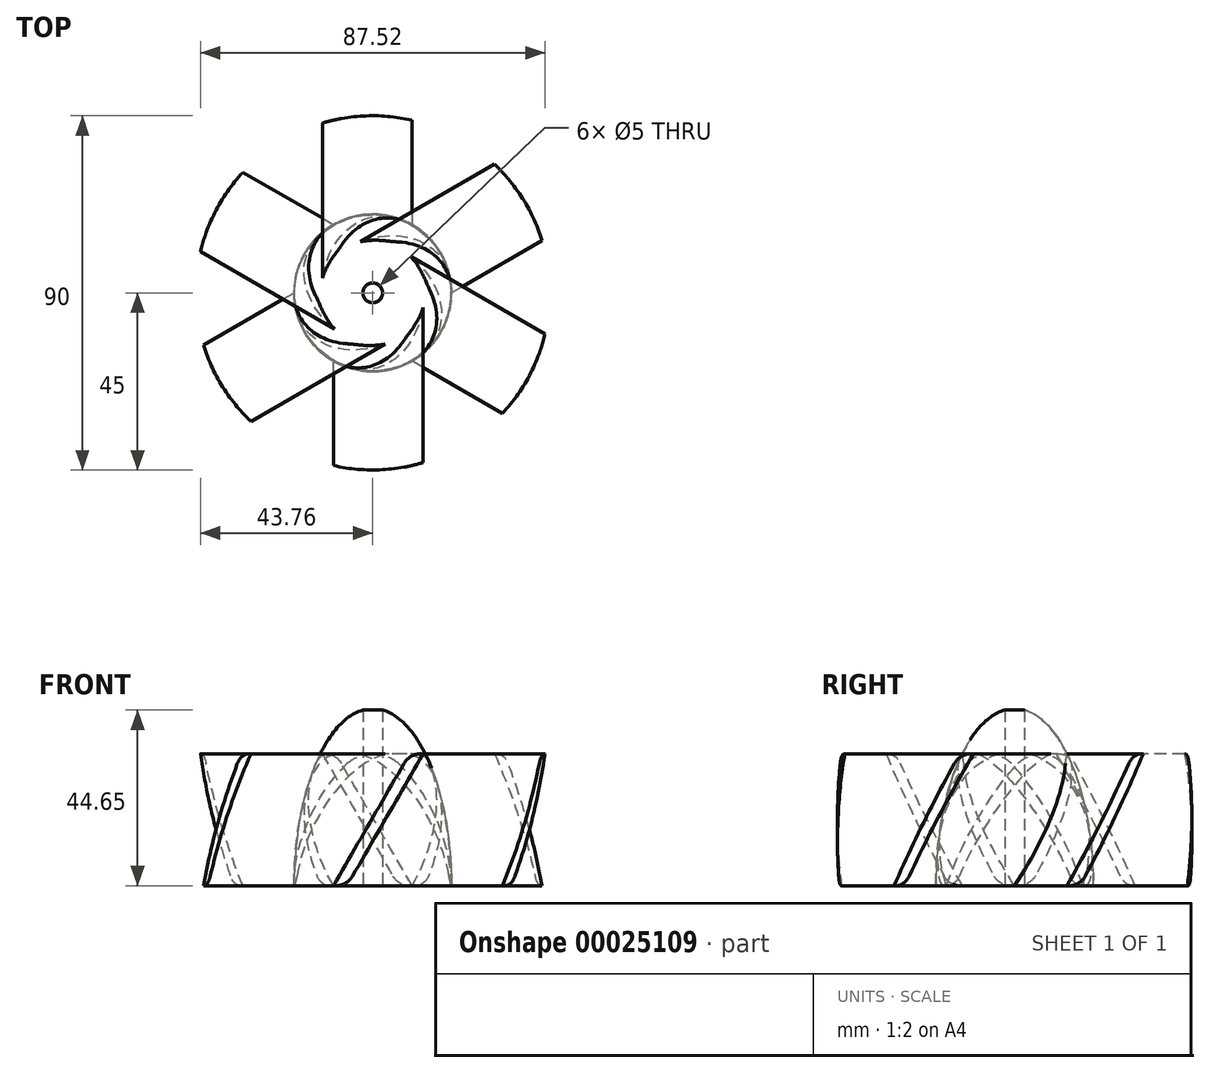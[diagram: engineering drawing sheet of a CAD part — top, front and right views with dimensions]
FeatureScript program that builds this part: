
annotation { "Feature Type Name" : "Feature", "Feature Type Description" : "" }
export const myFeature = defineFeature(function(context is Context, id is Id, definition is map)
    precondition{}
    {
        {
            var Q0;
            Q0=qCreatedBy(makeId("Front.planeOp"),FACE);
            var sketch = newSketch(context, id + "F0", { "sketchPlane" : qUnion([Q0])});
            skEllipticalArc(sketch, "E0", {});
            skLineSegment(sketch, "E1", {"start": v(-20, 0) * mm, "end": v(20, 0) * mm});
            skLineSegment(sketch, "E2", {"start": v(0, 0) * mm, "end": v(0, 45) * mm});
            const initialGuessF0  = {"E0": [0, 0, 0, 1, 0.045, 0.02, 4.71238898038469, 1.5707963267948966]};
            skSetInitialGuess(sketch, initialGuessF0);
            skSolve(sketch);
        }
        {
            var Q0;
            {var subQ0=sQuery(id+"F0.wireOp",EDGE,"E2");Q0=makeQuery(id+"F0.imprint","IMPRINT",FACE,{"disambiguationData":[TD([[makeQuery(id+"F0.imprint","IMPRINT",EDGE,{"derivedFrom":subQ0}),1.0]])]});}
            var Q1;
            Q1=sQuery(id+"F0.wireOp",EDGE,"E2");
            revolve(context, id + "F1", {"entities" : qUnion([Q0]), "axis" : qUnion([Q1]), "revolveType" : RevolveType.FULL});
        }
        {
            var Q0;
            Q0=qCreatedBy(makeId("Front.planeOp"),FACE);
            var sketch = newSketch(context, id + "F2", { "sketchPlane" : qUnion([Q0])});
            skLineSegment(sketch, "E3", {"start": v(-10, 0) * mm, "end": v(10.2, 35) * mm});
            skLineSegment(sketch, "E4", {"start": v(10.2, 35) * mm, "end": v(12.8, 33.5) * mm});
            skLineSegment(sketch, "E5", {"start": v(12.8, 33.5) * mm, "end": v(-6.54, 0) * mm});
            skLineSegment(sketch, "E6", {"start": v(-6.54, 0) * mm, "end": v(-10, 0) * mm});
            skSolve(sketch);
        }
        {
            var Q0;
            Q0 = qSketchRegion(id + "F2", true);
            extrude(context, id + "F3", {"entities" : qUnion([Q0]), "operationType" : NewBodyOperationType.ADD, "depth" : 50 * mm});
        }
        {
            var Q0;
            Q0=makeQuery(id+"F3.boolean.opBoolean","MERGE",FACE,{"derivedFrom":[makeQuery(id+"F1.opRevolve","SWEPT_FACE",FACE,{"disambiguationData":[OSD([sQuery(id+"F0.wireOp",EDGE,"E1")])]}),makeQuery(id+"F3.opExtrude","SWEPT_FACE",FACE,{"disambiguationData":[OSD([sQuery(id+"F2.wireOp",EDGE,"E6")])]})]});
            var sketch = newSketch(context, id + "F4", { "sketchPlane" : qUnion([Q0])});
            skCircle(sketch, "E7", {"center": v(0, 0) * mm, "radius": 55 * mm});
            skCircle(sketch, "E8", {"center": v(0, 0) * mm, "radius": 45 * mm});
            skSolve(sketch);
        }
        {
            var Q0;
            {var subQ0=sQuery(id+"F2.wireOp",EDGE,"E6");var subQ4=makeQuery(id+"F3.opExtrude","CAP_EDGE",EDGE,{"disambiguationData":[OSD([subQ0])],"isStart":false});Q0=makeQuery(id+"F4.imprint","IMPRINT",FACE,{"disambiguationData":[TD([[makeQuery(id+"F4.imprint","IMPRINT",EDGE,{"derivedFrom":subQ4}),1.0]])]});}
            var Q1;
            Q1=makeQuery(id+"F4.imprint","IMPRINT",FACE,{"disambiguationData":[TD([[makeQuery(id+"F4.imprint","IMPRINT",EDGE,{"derivedFrom":sQuery(id+"F4.wireOp",EDGE,"E7")}),1.0]])]});
            extrude(context, id + "F5", {"entities" : qUnion([Q0, Q1]), "operationType" : NewBodyOperationType.REMOVE, "oppositeDirection" : true, "depth" : 50 * mm});
        }
        {
            var Q0;
            Q0=makeQuery(id+"F3.opExtrude","SWEPT_EDGE",EDGE,{"disambiguationData":[OSD([sQuery(id+"F2.wireOp",EDGE,"E3"),sQuery(id+"F2.wireOp",EDGE,"E4")])]});
            var Q1;
            Q1=makeQuery(id+"F3.opExtrude","SWEPT_EDGE",EDGE,{"disambiguationData":[OSD([sQuery(id+"F2.wireOp",EDGE,"E5"),sQuery(id+"F2.wireOp",EDGE,"E6")])]});
            fillet(context, id + "F6", {"entities" : qUnion([Q0, Q1]), "radius" : 5 * mm, "tangentPropagation" : true, "allowEdgeOverflow" : false});
        }
        {
            var Q0;
            Q0=makeQuery(id+"F1.opRevolve","SWEPT_BODY",BODY,{"disambiguationData":[OSD([sQuery(id+"F0.wireOp",EDGE,"E0"),sQuery(id+"F0.wireOp",EDGE,"E1"),sQuery(id+"F0.wireOp",EDGE,"E2")])]});
            var Q1;
            Q1=makeQuery(id+"F1.opRevolve","SWEPT_EDGE",EDGE,{"disambiguationData":[OSD([sQuery(id+"F0.wireOp",EDGE,"E0"),sQuery(id+"F0.wireOp",EDGE,"E1")])]});
            circularPattern(context, id + "F7", {"entities" : qUnion([Q0]), "axis" : qUnion([Q1]), "angle" : 360 * degree, "instanceCount" : 6, "equalSpace" : true});
        }
        {
            var Q0;
            Q0=makeQuery(id+"F7.opPattern","COPY",FACE,{"derivedFrom":makeQuery(id+"F3.boolean.opBoolean","MERGE",FACE,{"derivedFrom":[makeQuery(id+"F1.opRevolve","SWEPT_FACE",FACE,{"disambiguationData":[OSD([sQuery(id+"F0.wireOp",EDGE,"E1")])]}),makeQuery(id+"F3.opExtrude","SWEPT_FACE",FACE,{"disambiguationData":[OSD([sQuery(id+"F2.wireOp",EDGE,"E6")])]})]}),"instanceName":"3"});
            var sketch = newSketch(context, id + "F8", { "sketchPlane" : qUnion([Q0])});
            skCircle(sketch, "E9", {"center": v(0, 0) * mm, "radius": 2.5 * mm});
            skSolve(sketch);
        }
        {
            var Q0;
            Q0=makeQuery(id+"F8.imprint","IMPRINT",FACE,{"disambiguationData":[TD([[makeQuery(id+"F8.imprint","IMPRINT",EDGE,{"derivedFrom":sQuery(id+"F8.wireOp",EDGE,"E9")}),1.0]])]});
            extrude(context, id + "F9", {"entities" : qUnion([Q0]), "operationType" : NewBodyOperationType.REMOVE, "endBound" : BoundingType.THROUGH_ALL, "oppositeDirection" : true, "depth" : 25 * mm});
        }
    });
